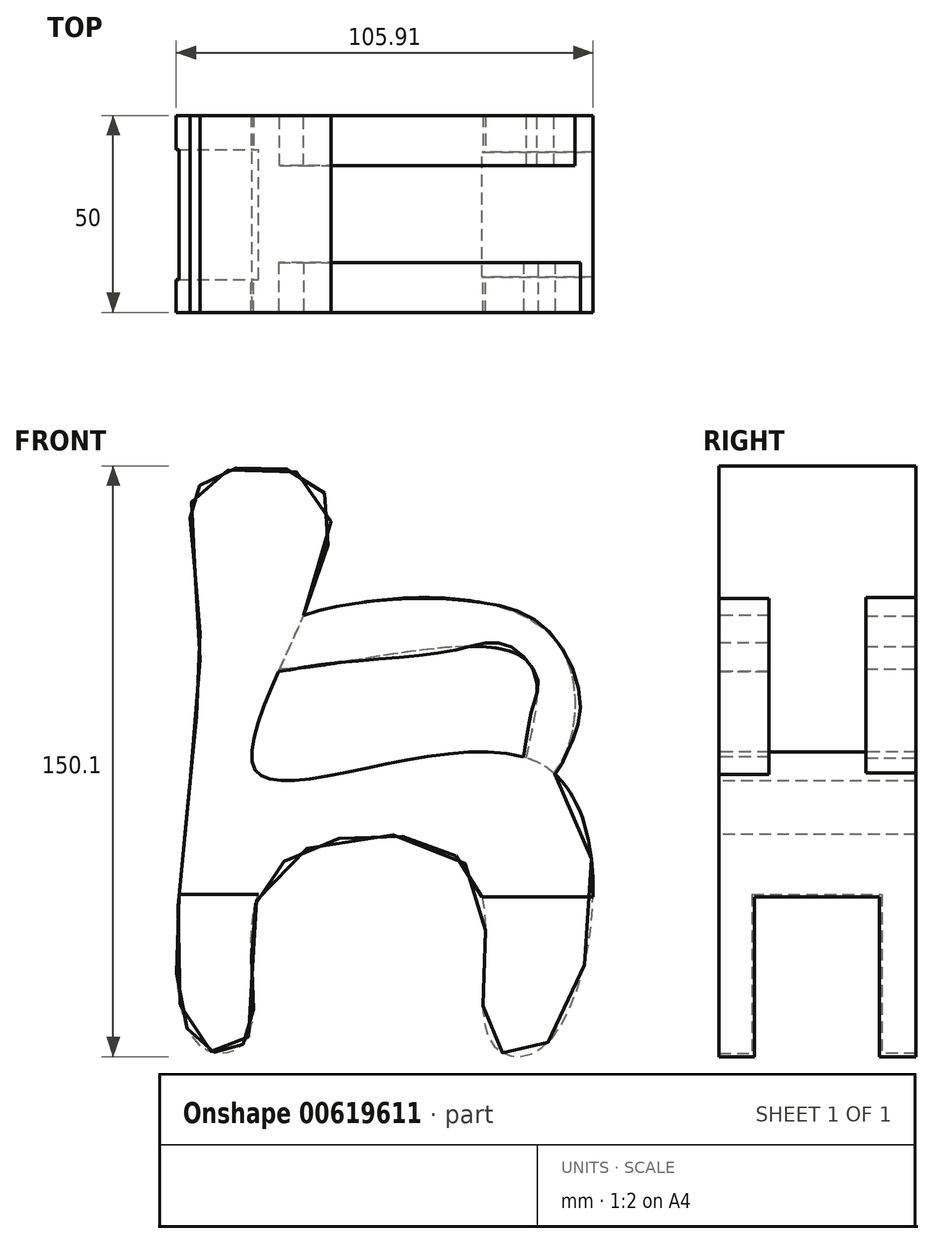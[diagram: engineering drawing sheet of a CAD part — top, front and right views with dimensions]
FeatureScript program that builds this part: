
annotation { "Feature Type Name" : "Feature", "Feature Type Description" : "" }
export const myFeature = defineFeature(function(context is Context, id is Id, definition is map)
    precondition{}
    {
        {
            var Q0;
            Q0=qCreatedBy(makeId("Front.planeOp"),FACE);
            var sketch = newSketch(context, id + "F0", { "sketchPlane" : qUnion([Q0])});
            skFitSpline(sketch, "E0", {"points": [v(-51.68, 47.12) * mm, v(-53.57, -57.5) * mm, v(-39.74, -57.8) * mm, v(-34.4, -16.65) * mm, v(16.18, -13.82) * mm, v(21.52, -57.18) * mm, v(36.91, -58.43) * mm, v(35.66, 11.62) * mm, v(-37.54, 10.37) * mm, v(-19, 78.54) * mm, v(-49.8, 84.51) * mm, v(-51.68, 47.12) * mm]});
            skSolve(sketch);
        }
        {
            var Q0;
            Q0=makeQuery(id+"F0.imprint","IMPRINT",FACE,{"disambiguationData":[TD([[makeQuery(id+"F0.imprint","IMPRINT",EDGE,{"derivedFrom":sQuery(id+"F0.wireOp",EDGE,"E0")}),1.0]])]});
            extrude(context, id + "F1", {"entities" : qUnion([Q0]), "depth" : 50 * mm, "offsetDistance" : 25.4 * mm});
        }
        {
            var Q0;
            Q0=qCreatedBy(makeId("Right.planeOp"),FACE);
            var sketch = newSketch(context, id + "F2", { "sketchPlane" : qUnion([Q0])});
            skLineSegment(sketch, "E1.bottom", {"start": v(-41.63, -21.05) * mm, "end": v(-8.64, -21.05) * mm});
            skLineSegment(sketch, "E1.top", {"start": v(-41.63, -67.55) * mm, "end": v(-8.64, -67.55) * mm});
            skLineSegment(sketch, "E1.left", {"start": v(-41.63, -21.05) * mm, "end": v(-41.63, -67.55) * mm});
            skLineSegment(sketch, "E1.right", {"start": v(-8.64, -21.05) * mm, "end": v(-8.64, -67.55) * mm});
            skSolve(sketch);
        }
        {
            var Q0;
            Q0=makeQuery(id+"F2.imprint","IMPRINT",FACE,{"disambiguationData":[TD([[makeQuery(id+"F2.imprint","IMPRINT",EDGE,{"derivedFrom":sQuery(id+"F2.wireOp",EDGE,"E1.bottom")}),-1.0]])]});
            extrude(context, id + "F3", {"entities" : qUnion([Q0]), "operationType" : NewBodyOperationType.REMOVE, "oppositeDirection" : true, "depth" : 72.64 * mm, "offsetDistance" : 25.4 * mm});
        }
        {
            var Q0;
            Q0=qCreatedBy(makeId("Right.planeOp"),FACE);
            var sketch = newSketch(context, id + "F4", { "sketchPlane" : qUnion([Q0])});
            skLineSegment(sketch, "E2.bottom", {"start": v(-41, -21.68) * mm, "end": v(-9.27, -21.68) * mm});
            skLineSegment(sketch, "E2.top", {"start": v(-41, -65.66) * mm, "end": v(-9.27, -65.66) * mm});
            skLineSegment(sketch, "E2.left", {"start": v(-41, -21.68) * mm, "end": v(-41, -65.66) * mm});
            skLineSegment(sketch, "E2.right", {"start": v(-9.27, -21.68) * mm, "end": v(-9.27, -65.66) * mm});
            skSolve(sketch);
        }
        {
            var Q0;
            Q0=makeQuery(id+"F4.imprint","IMPRINT",FACE,{"disambiguationData":[TD([[makeQuery(id+"F4.imprint","IMPRINT",EDGE,{"derivedFrom":sQuery(id+"F4.wireOp",EDGE,"E2.bottom")}),-1.0]])]});
            extrude(context, id + "F5", {"entities" : qUnion([Q0]), "operationType" : NewBodyOperationType.REMOVE, "depth" : 56.13 * mm, "offsetDistance" : 25.4 * mm});
        }
        {
            var Q0;
            Q0=qCreatedBy(makeId("Front.planeOp"),FACE);
            var sketch = newSketch(context, id + "F6", { "sketchPlane" : qUnion([Q0])});
            skFitSpline(sketch, "E3", {"points": [v(-35.97, 44.61) * mm, v(35.66, 46.5) * mm, v(38.17, 9.74) * mm, v(30.95, 7.85) * mm, v(31.26, 38.33) * mm, v(-36.6, 36.76) * mm, v(-35.97, 44.61) * mm]});
            skSolve(sketch);
        }
        {
            var Q0;
            Q0=makeQuery(id+"F6.imprint","IMPRINT",FACE,{"disambiguationData":[TD([[makeQuery(id+"F6.imprint","IMPRINT",EDGE,{"derivedFrom":sQuery(id+"F6.wireOp",EDGE,"E3")}),-1.0]])]});
            extrude(context, id + "F7", {"entities" : qUnion([Q0]), "operationType" : NewBodyOperationType.ADD, "depth" : 12.7 * mm, "offsetDistance" : 25.4 * mm});
        }
        {
            var Q0;
            Q0=makeQuery(id+"F1.opExtrude","CAP_FACE",FACE,{"disambiguationData":[OSD([sQuery(id+"F0.wireOp",EDGE,"E0")])],"isStart":false});
            cPlane(context, id + "F8", {"entities" : qUnion([Q0]), "cplaneType" : CPlaneType.OFFSET, "offset" : 0 * mm, "width" : 152.4 * mm, "height" : 152.4 * mm});
        }
        {
            var Q0;
            Q0=qCreatedBy(id+"F8.planeOp",FACE);
            var sketch = newSketch(context, id + "F9", { "sketchPlane" : qUnion([Q0])});
            skFitSpline(sketch, "E4", {"points": [v(-27.92, 48.88) * mm, v(-14.34, 52.59) * mm, v(3.57, 54.13) * mm, v(19.3, 53.2) * mm, v(35.98, 46.72) * mm, v(44.93, 27.27) * mm, v(41.53, 14.93) * mm, v(37.21, 8.14) * mm, v(30.42, 5.67) * mm, v(30.73, 15.24) * mm, v(32.9, 26.96) * mm, v(34.13, 33.76) * mm, v(26.1, 42.4) * mm, v(14.99, 41.47) * mm, v(-6.62, 38.7) * mm, v(-26.37, 36.53) * mm, v(-33.17, 36.23) * mm, v(-32.24, 44.87) * mm, v(-27.92, 48.88) * mm]});
            skSolve(sketch);
        }
        {
            var Q0;
            Q0=makeQuery(id+"F9.imprint","IMPRINT",FACE,{"disambiguationData":[TD([[makeQuery(id+"F9.imprint","IMPRINT",EDGE,{"derivedFrom":sQuery(id+"F9.wireOp",EDGE,"E4")}),-1.0]])]});
            extrude(context, id + "F10", {"entities" : qUnion([Q0]), "operationType" : NewBodyOperationType.ADD, "oppositeDirection" : true, "depth" : 12.7 * mm, "offsetDistance" : 25.4 * mm});
        }
    });
